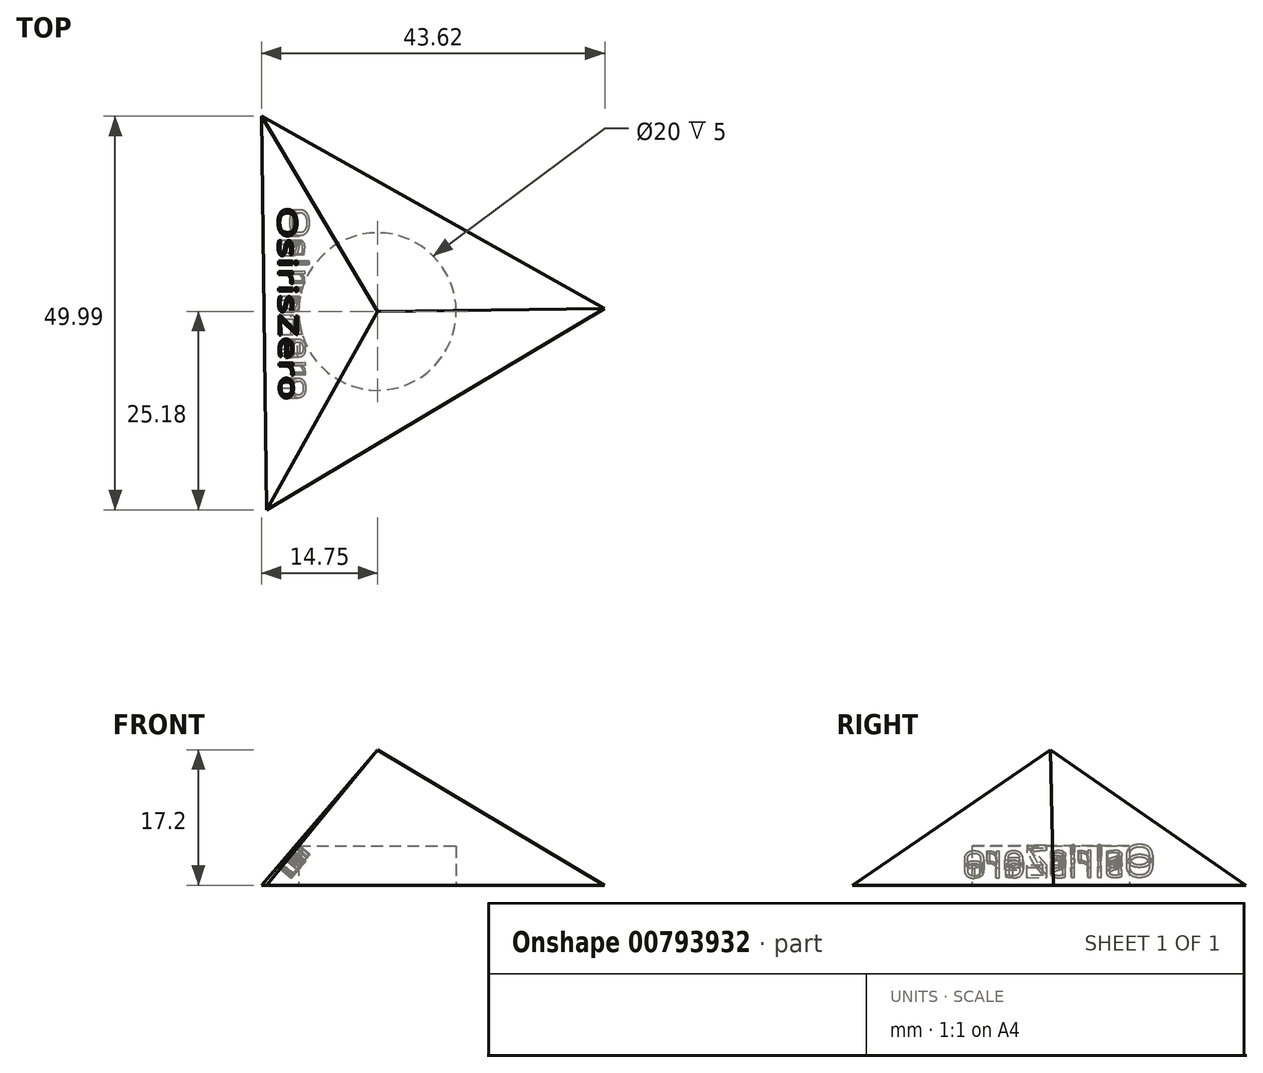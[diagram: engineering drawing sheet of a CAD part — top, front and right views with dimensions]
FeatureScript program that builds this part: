
annotation { "Feature Type Name" : "Feature", "Feature Type Description" : "" }
export const myFeature = defineFeature(function(context is Context, id is Id, definition is map)
    precondition{}
    {
        {
            var Q0;
            Q0=qCreatedBy(makeId("Top.planeOp"),FACE);
            var sketch = newSketch(context, id + "F0", { "sketchPlane" : qUnion([Q0])});
            skCircle(sketch, "E0.cCircle", {"center": v(0, 0) * mm, "radius": 14.43 * mm, "construction": true});
            skLineSegment(sketch, "E0.0", {"start": v(-14.75, 24.81) * mm, "end": v(28.87, 0.37) * mm});
            skLineSegment(sketch, "E0.1", {"start": v(28.87, 0.37) * mm, "end": v(-14.11, -25.18) * mm});
            skLineSegment(sketch, "E0.2", {"start": v(-14.11, -25.18) * mm, "end": v(-14.75, 24.81) * mm});
            skPoint(sketch, "E0.0.midPoint", {"position": v(7.06, 12.6) * mm});
            skSolve(sketch);
        }
        {
            var Q0;
            Q0=makeQuery(id+"F0.imprint","IMPRINT",FACE,{"disambiguationData":[TD([[makeQuery(id+"F0.imprint","IMPRINT",EDGE,{"derivedFrom":sQuery(id+"F0.wireOp",EDGE,"E0.0")}),-1.0]])]});
            extrude(context, id + "F1", {"entities" : qUnion([Q0]), "depth" : 30 * mm, "offsetDistance" : 25 * mm, "hasDraft" : true, "draftAngle" : 40 * degree, "draftPullDirection" : true});
        }
        {
            var Q0;
            Q0=makeQuery(id+"F1.opExtrude","SWEPT_FACE",FACE,{"disambiguationData":[OSD([sQuery(id+"F0.wireOp",EDGE,"E0.2")])]});
            var sketch = newSketch(context, id + "F2", { "sketchPlane" : qUnion([Q0])});
            skText(sketch, "E1", { "text": "OsirisZero", "fontName": "OpenSans-Regular.ttf"});
            const initialGuessF2  = {"E1": [-0.01339, -0.00632, 1, 0, 0.00369]};
            skSetInitialGuess(sketch, initialGuessF2);
            skSolve(sketch);
        }
        {
            var Q0;
            Q0=makeQuery(id+"F1.opExtrude","CAP_FACE",FACE,{"disambiguationData":[OSD([sQuery(id+"F0.wireOp",EDGE,"E0.0"),sQuery(id+"F0.wireOp",EDGE,"E0.1"),sQuery(id+"F0.wireOp",EDGE,"E0.2")])],"isStart":true});
            var sketch = newSketch(context, id + "F3", { "sketchPlane" : qUnion([Q0])});
            skCircle(sketch, "E2", {"center": v(0, 0) * mm, "radius": 10 * mm});
            skSolve(sketch);
        }
        {
            var Q0;
            Q0=makeQuery(id+"F3.imprint","IMPRINT",FACE,{"disambiguationData":[TD([[makeQuery(id+"F3.imprint","IMPRINT",EDGE,{"derivedFrom":sQuery(id+"F3.wireOp",EDGE,"E2")}),1.0]])]});
            extrude(context, id + "F4", {"entities" : qUnion([Q0]), "operationType" : NewBodyOperationType.REMOVE, "oppositeDirection" : true, "depth" : 5 * mm, "offsetDistance" : 25 * mm});
        }
        {
            var Q0;
            Q0 = qSketchRegion(id + "F2", true);
            extrude(context, id + "F5", {"entities" : qUnion([Q0]), "operationType" : NewBodyOperationType.REMOVE, "oppositeDirection" : true, "depth" : 2 * mm, "offsetDistance" : 25 * mm});
        }
    });
